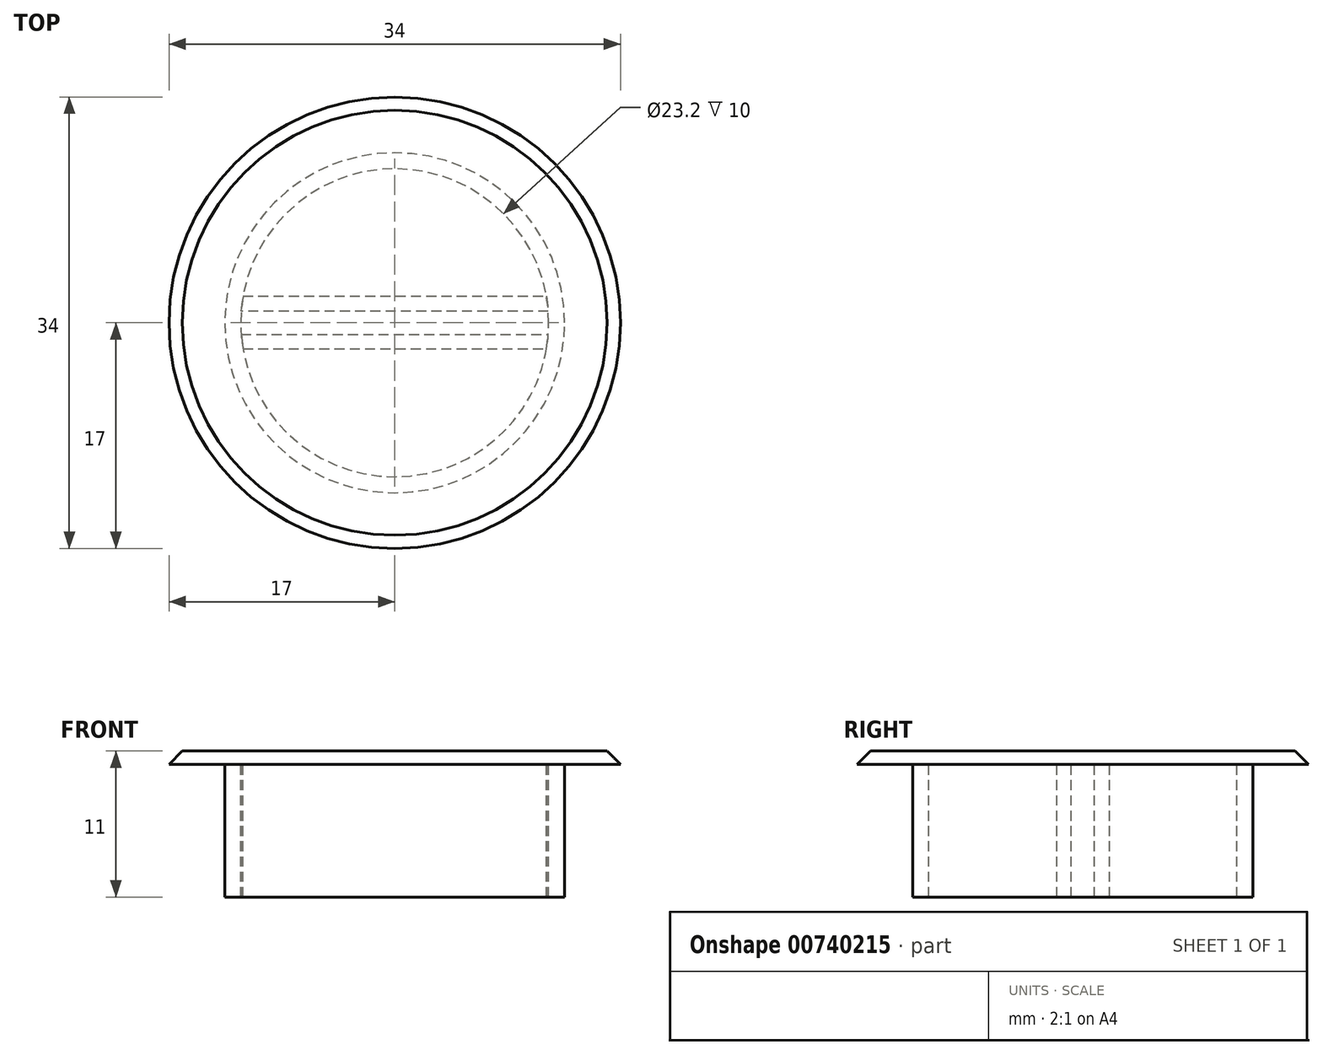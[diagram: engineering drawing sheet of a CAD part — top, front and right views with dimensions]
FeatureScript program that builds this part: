
annotation { "Feature Type Name" : "Feature", "Feature Type Description" : "" }
export const myFeature = defineFeature(function(context is Context, id is Id, definition is map)
    precondition{}
    {
        {
            var Q0;
            Q0=qCreatedBy(makeId("Front.planeOp"),FACE);
            var sketch = newSketch(context, id + "F0", { "sketchPlane" : qUnion([Q0])});
            skLineSegment(sketch, "E0", {"start": v(0, 10) * mm, "end": v(12.8, 10) * mm});
            skLineSegment(sketch, "E1", {"start": v(12.8, 10) * mm, "end": v(12.8, 0) * mm});
            skLineSegment(sketch, "E2", {"start": v(0, 11) * mm, "end": v(0, 10) * mm});
            skLineSegment(sketch, "E3", {"start": v(0, 10) * mm, "end": v(18, 10) * mm});
            skLineSegment(sketch, "E4", {"start": v(11.6, 10) * mm, "end": v(11.6, 0) * mm});
            skLineSegment(sketch, "E5", {"start": v(0, 8.27) * mm, "end": v(11.6, 8.27) * mm, "construction": true});
            skLineSegment(sketch, "E6", {"start": v(11.6, 0) * mm, "end": v(12.8, 0) * mm});
            skLineSegment(sketch, "E7", {"start": v(11.6, 10) * mm, "end": v(12.8, 10) * mm});
            skLineSegment(sketch, "E8", {"start": v(0, 11) * mm, "end": v(18, 11) * mm});
            skLineSegment(sketch, "E9", {"start": v(18, 11) * mm, "end": v(18, 10) * mm});
            skSolve(sketch);
        }
        {
            var Q0;
            {var subQ1=sQuery(id+"F0.wireOp",EDGE,"E2");Q0=makeQuery(id+"F0.imprint","IMPRINT",FACE,{"disambiguationData":[TD([[makeQuery(id+"F0.imprint","IMPRINT",EDGE,{"derivedFrom":subQ1}),1.0]])]});}
            var Q1;
            {var subQ0=sQuery(id+"F0.wireOp",EDGE,"E1");Q1=makeQuery(id+"F0.imprint","IMPRINT",FACE,{"disambiguationData":[TD([[makeQuery(id+"F0.imprint","IMPRINT",EDGE,{"derivedFrom":subQ0}),-1.0]])]});}
            var Q2;
            Q2=sQuery(id+"F0.wireOp",EDGE,"E2");
            revolve(context, id + "F1", {"surfaceOperationType" : NewSurfaceOperationType.NEW, "entities" : qUnion([Q0, Q1]), "axis" : qUnion([Q2]), "revolveType" : RevolveType.FULL});
        }
        {
            var Q0;
            Q0=makeQuery(id+"F1.opRevolve","SWEPT_EDGE",EDGE,{"disambiguationData":[OSD([sQuery(id+"F0.wireOp",EDGE,"E8"),sQuery(id+"F0.wireOp",EDGE,"E9")])]});
            chamfer(context, id + "F2", {"entities" : qUnion([Q0]), "width" : 2 * mm, "tangentPropagation" : true});
        }
        {
            var Q0;
            Q0=makeQuery(id+"F1.opRevolve","SWEPT_FACE",FACE,{"disambiguationData":[OSD([sQuery(id+"F0.wireOp",EDGE,"E0")])]});
            var sketch = newSketch(context, id + "F3", { "sketchPlane" : qUnion([Q0])});
            skLineSegment(sketch, "E10", {"start": v(-11.57, 0.88) * mm, "end": v(11.57, 0.88) * mm});
            skLineSegment(sketch, "E11", {"start": v(11.57, -0.87) * mm, "end": v(-11.57, -0.88) * mm});
            skLineSegment(sketch, "E12", {"start": v(0, 0) * mm, "end": v(0, -0.88) * mm, "construction": true});
            skLineSegment(sketch, "E13", {"start": v(0, 0) * mm, "end": v(0, 0.88) * mm, "construction": true});
            skLineSegment(sketch, "E14", {"start": v(-11.57, 0.88) * mm, "end": v(-11.43, 1.97) * mm});
            skLineSegment(sketch, "E15", {"start": v(-11.43, 1.97) * mm, "end": v(11.43, 1.97) * mm});
            skLineSegment(sketch, "E16", {"start": v(11.43, 1.97) * mm, "end": v(11.57, 0.88) * mm});
            skLineSegment(sketch, "E17", {"start": v(-11.57, -0.88) * mm, "end": v(-11.42, -2.02) * mm});
            skLineSegment(sketch, "E18", {"start": v(-11.42, -2.02) * mm, "end": v(11.42, -2.02) * mm});
            skLineSegment(sketch, "E19", {"start": v(11.42, -2.02) * mm, "end": v(11.57, -0.88) * mm});
            skLineSegment(sketch, "E20", {"start": v(-11.57, -0.88) * mm, "end": v(11.57, -0.87) * mm});
            skSolve(sketch);
        }
        {
            var Q0;
            Q0=makeQuery(id+"F3.imprint","IMPRINT",FACE,{"disambiguationData":[TD([[makeQuery(id+"F3.imprint","IMPRINT",EDGE,{"derivedFrom":sQuery(id+"F3.wireOp",EDGE,"E10")}),1.0]])]});
            var Q1;
            Q1=makeQuery(id+"F3.imprint","IMPRINT",FACE,{"disambiguationData":[TD([[makeQuery(id+"F3.imprint","IMPRINT",EDGE,{"derivedFrom":sQuery(id+"F3.wireOp",EDGE,"E17")}),1.0]])]});
            extrude(context, id + "F4", {"entities" : qUnion([Q0, Q1]), "depth" : 10 * mm, "offsetDistance" : 25 * mm});
        }
    });
